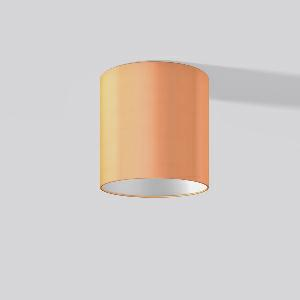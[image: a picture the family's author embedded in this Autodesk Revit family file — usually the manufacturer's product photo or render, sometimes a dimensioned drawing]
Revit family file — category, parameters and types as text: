
# Revit family: toledo_flatliner_901628_002_1_a1e6
name_source: partatom
category: Lighting Fixtures
units: mm (PartAtom-declared; Revit-internal decimal feet)

## family parameters
Cut with Voids When Loaded = No
Host = Face
Light Source = No
Part Type = Normal
Room Calculation Point = No
Round Connector Dimension = Use Diameter
Shared = No

## types (1)
- 982299.002 (1 x LED Modul 840, 360 lm, 4000)
    Apparent Load = 5 VA
    CIE Flux Codes = 56 78 92 81 100
    Color Rendering = 80
    Color Temperature = 4000
    Default Elevation = 1800 mm
    Description = Series: TOLEDO FLATLINER
Decorative ceiling luminaire for interior decoration. Base luminaire prepared for the installation of fabric lampshade. Cylinder housing sheet steel, powder-coated. Housing: die cast aluminium and sheet steel, powder-coated. Bezel ring: die-cast aluminium, powder-coated. Lightguide and diffuser made of non-yellowing plastic (PMMA) opal matt. Modular design: With the basic luminaire, a square or cylindrical fabric lampshade must always be ordered separately. Fabric lampshades can be fitted to the basic luminaire without tools. Order satin finish diffuser as separate accessory. 
Colour: white
Diameter: 160 mm
Height: 65 mm
Lamp: LED
Socket: without socket
Colour temperature: 4000K
Colour rendering index (CRI): 80
System power: 5 W
Rated luminous flux: 360 lm
Luminous efficiency: 72 lm/W
Control gear: Regulated power supply
Protection class: II
Type of protection: IP 40
    Height = 65 mm
    Lamp = 1 x LED Modul 840
    Lamp Light Flux = 360 lm
    Lamp count = 1
    Length = 160 mm
    Lifetime = 50000 h
    Luminous efficacy = 72 lm/W
    Manufacturer = RZB
    ModVariant = No
    Model = 901628.002.1
    Mounting Place = Ceiling
    Mounting Type = Surface mounted
    Number of Poles = 1
    OnlyDefault = Yes
    Power Factor = 1
    Product Name = TOLEDO FLATLINER
    Product group = Surface mounted ceiling Fabric lampshade luminaires
    ProductGroupID = 313
    Protection Class = Protection class II
    Protection Degree = IP 40
    RLX_Detail_Level = 1
    RLX_Emergency_Light_Flux = 0 lm
    RLX_Emergency_Type = 0
    RLX_Emergency_Type_DB = No
    RlxData = <blob elided: 62233 chars, md5=4dc27d84>
    Socket = socket
    Standby Power = 0 W
    System Light Flux = 360 lm
    System Power = 5 W
    Type Image = toledo_flatliner_anbau_rund_orange_odeckel.jpg
    URL = http://relux.com
    VarID = 982299_002_f7b2
    Voltage = 230 V
    Voltage Range = 220-240 V
    Weight = 0.00 kg
    Width = 0 mm  [stored 0 ft]

note: [stored X ft] marks values corroborated as IEEE doubles in the binary element streams (Revit-internal decimal feet)

## geometry (parser evidence)
native form markers: Blend x4, Sweep x10
no freeform markers — native parametric forms only
